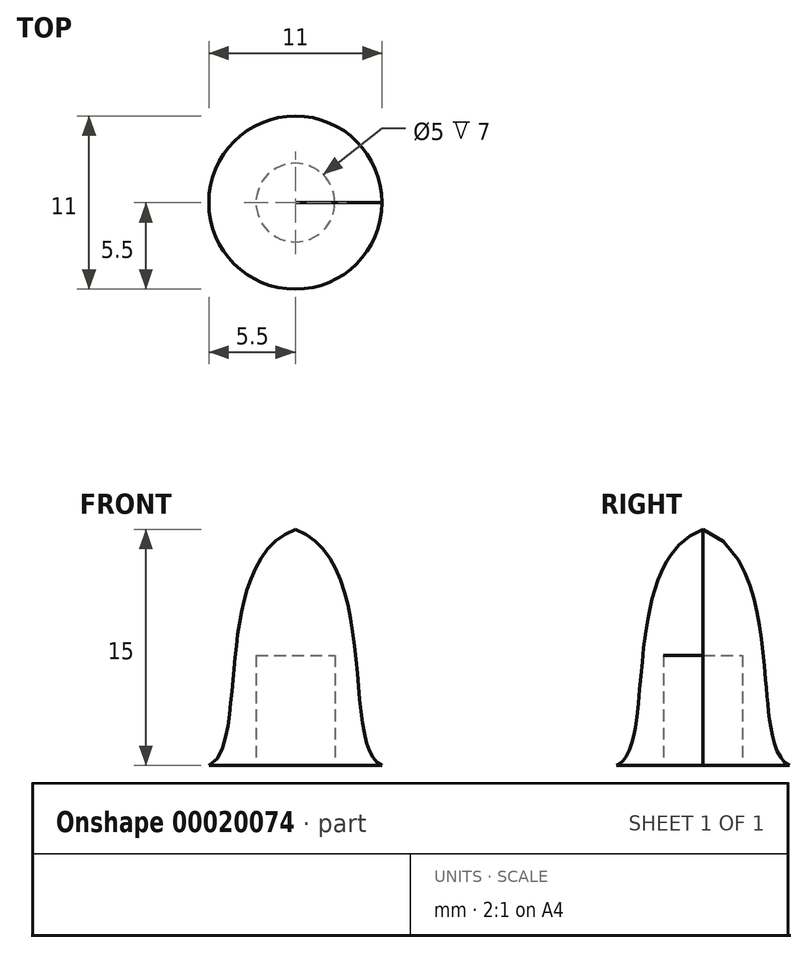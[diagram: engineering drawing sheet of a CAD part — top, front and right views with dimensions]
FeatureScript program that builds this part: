
annotation { "Feature Type Name" : "Feature", "Feature Type Description" : "" }
export const myFeature = defineFeature(function(context is Context, id is Id, definition is map)
    precondition{}
    {
        {
            var Q0;
            Q0=qCreatedBy(makeId("Front.planeOp"),FACE);
            var sketch = newSketch(context, id + "F0", { "sketchPlane" : qUnion([Q0])});
            skLineSegment(sketch, "E0.rect.bottom", {"start": v(0, -7.5) * mm, "end": v(-3, -7.5) * mm});
            skLineSegment(sketch, "E0.rect.right", {"start": v(-5.5, -0.5) * mm, "end": v(-5.5, 7.5) * mm});
            skPoint(sketch, "E0.rect.middle", {"position": v(-2.75, 0) * mm});
            skFitSpline(sketch, "E1", {"points": [v(-5.5, 7.5) * mm, v(0, -7.5) * mm], "startDerivative": vector(16.36, -6.03) * mm, "endDerivative": vector(7.94, -3.3) * mm});
            skLineSegment(sketch, "E2.top", {"start": v(-5.5, -0.5) * mm, "end": v(-3, -0.5) * mm});
            skLineSegment(sketch, "E2.right", {"start": v(-3, -7.5) * mm, "end": v(-3, -0.5) * mm});
            skPoint(sketch, "E0.rect.top.start.orphan", {"position": v(0, 7.5) * mm});
            skPoint(sketch, "E2.bottom.start.orphan", {"position": v(-5.5, -7.5) * mm});
            skSolve(sketch);
        }
        {
            var Q0;
            Q0 = qSketchRegion(id + "F0", true);
            var Q1;
            Q1=sQuery(id+"F0.wireOp",EDGE,"E0.rect.right");
            revolve(context, id + "F1", {"entities" : qUnion([Q0]), "axis" : qUnion([Q1]), "revolveType" : RevolveType.FULL});
        }
    });
